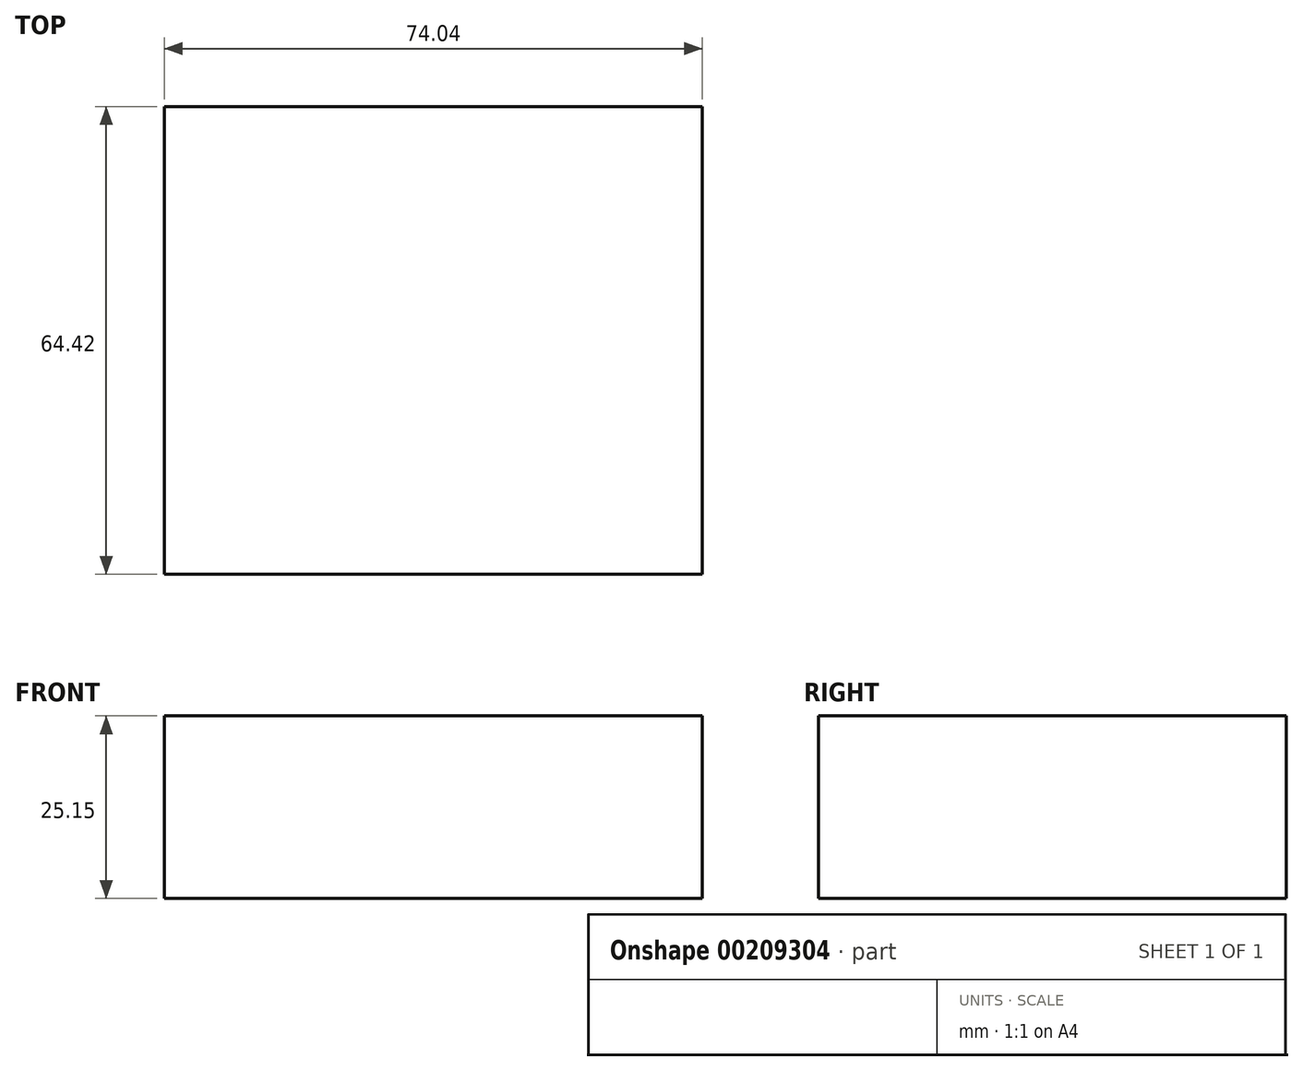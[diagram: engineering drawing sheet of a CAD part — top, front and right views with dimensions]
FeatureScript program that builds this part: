
annotation { "Feature Type Name" : "Feature", "Feature Type Description" : "" }
export const myFeature = defineFeature(function(context is Context, id is Id, definition is map)
    precondition{}
    {
        {
            var Q0;
            Q0=qCreatedBy(makeId("Top.planeOp"),FACE);
            var sketch = newSketch(context, id + "F0", { "sketchPlane" : qUnion([Q0])});
            skLineSegment(sketch, "E0.bottom", {"start": v(-36.73, 33.96) * mm, "end": v(37.3, 33.96) * mm});
            skLineSegment(sketch, "E0.top", {"start": v(-36.73, -30.46) * mm, "end": v(37.3, -30.46) * mm});
            skLineSegment(sketch, "E0.left", {"start": v(-36.73, 33.96) * mm, "end": v(-36.73, -30.46) * mm});
            skLineSegment(sketch, "E0.right", {"start": v(37.3, 33.96) * mm, "end": v(37.3, -30.46) * mm});
            skSolve(sketch);
        }
        {
            var Q0;
            Q0=makeQuery(id+"F0.imprint","IMPRINT",FACE,{"disambiguationData":[TD([[makeQuery(id+"F0.imprint","IMPRINT",EDGE,{"derivedFrom":sQuery(id+"F0.wireOp",EDGE,"E0.bottom")}),-1.0]])]});
            extrude(context, id + "F1", {"entities" : qUnion([Q0]), "depth" : 25.15 * mm});
        }
    });
